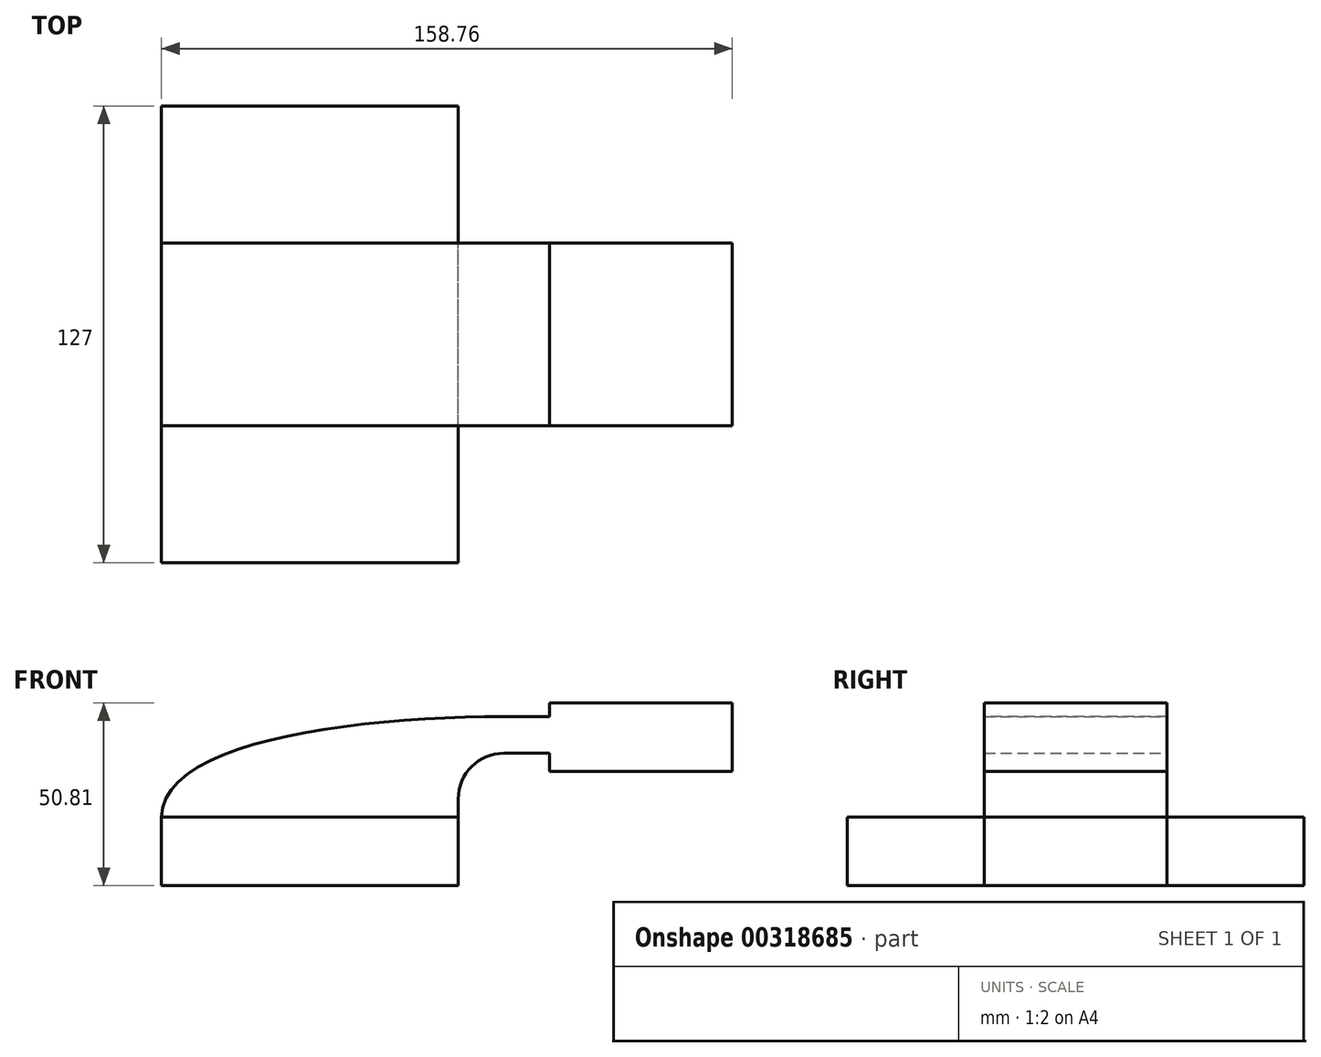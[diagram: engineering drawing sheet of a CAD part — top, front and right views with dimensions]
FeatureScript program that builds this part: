
annotation { "Feature Type Name" : "Feature", "Feature Type Description" : "" }
export const myFeature = defineFeature(function(context is Context, id is Id, definition is map)
    precondition{}
    {
        {
            var Q0;
            Q0=qCreatedBy(makeId("Front.planeOp"),FACE);
            var sketch = newSketch(context, id + "F0", { "sketchPlane" : qUnion([Q0])});
            skLineSegment(sketch, "E0.bottom", {"start": v(-41.27, -9.53) * mm, "end": v(41.28, -9.53) * mm});
            skLineSegment(sketch, "E0.top", {"start": v(-41.28, 9.53) * mm, "end": v(41.27, 9.53) * mm});
            skLineSegment(sketch, "E0.left", {"start": v(-41.27, -9.53) * mm, "end": v(-41.28, 9.52) * mm});
            skLineSegment(sketch, "E0.right", {"start": v(41.28, -9.53) * mm, "end": v(41.27, 9.52) * mm});
            skPoint(sketch, "E0.middle", {"position": v(0, 0) * mm});
            skLineSegment(sketch, "E1.bottom", {"start": v(66.68, 41.28) * mm, "end": v(117.48, 41.28) * mm});
            skLineSegment(sketch, "E1.top", {"start": v(66.68, 22.23) * mm, "end": v(117.48, 22.23) * mm});
            skLineSegment(sketch, "E1.left", {"start": v(66.68, 41.28) * mm, "end": v(66.68, 22.23) * mm});
            skLineSegment(sketch, "E1.right", {"start": v(117.48, 41.28) * mm, "end": v(117.48, 22.23) * mm});
            skPoint(sketch, "E1.middle", {"position": v(92.08, 31.75) * mm});
            skLineSegment(sketch, "E2", {"start": v(41.28, 9.52) * mm, "end": v(41.28, 14.6) * mm});
            skArc(sketch, "E3", {"start": v(41.27, 14.6) * mm, "mid": v(45, 23.59) * mm, "end": v(53.98, 27.3) * mm});
            skLineSegment(sketch, "E4", {"start": v(53.98, 27.3) * mm, "end": v(79.38, 27.3) * mm});
            skLineSegment(sketch, "E5.0", {"start": v(53.98, 37.46) * mm, "end": v(79.38, 37.46) * mm});
            skArc(sketch, "E5.1", {"start": v(31.11, 14.6) * mm, "mid": v(37.81, 30.77) * mm, "end": v(53.98, 37.47) * mm});
            skLineSegment(sketch, "E5.2", {"start": v(31.12, 9.53) * mm, "end": v(31.12, 14.6) * mm});
            skLineSegment(sketch, "E6", {"start": v(79.38, 41.28) * mm, "end": v(79.38, 22.23) * mm});
            skFitSpline(sketch, "E7", {"points": [v(-41.28, 9.53) * mm, v(53.98, 37.47) * mm], "startDerivative": vector(0.7, 63.96) * mm, "endDerivative": vector(121.55, -0.15) * mm});
            skSolve(sketch);
        }
        {
            var Q0;
            Q0=makeQuery(id+"F0.imprint","IMPRINT",FACE,{"disambiguationData":[TD([[makeQuery(id+"F0.imprint","IMPRINT",EDGE,{"derivedFrom":sQuery(id+"F0.wireOp",EDGE,"E0.bottom")}),1.0]])]});
            extrude(context, id + "F1", {"entities" : qUnion([Q0]), "endBound" : BoundingType.SYMMETRIC, "depth" : 127 * mm});
        }
        {
            var Q0;
            Q0 = qSketchRegion(id + "F0", true);
            extrude(context, id + "F2", {"entities" : qUnion([Q0]), "endBound" : BoundingType.SYMMETRIC, "depth" : 50.8 * mm});
        }
    });
